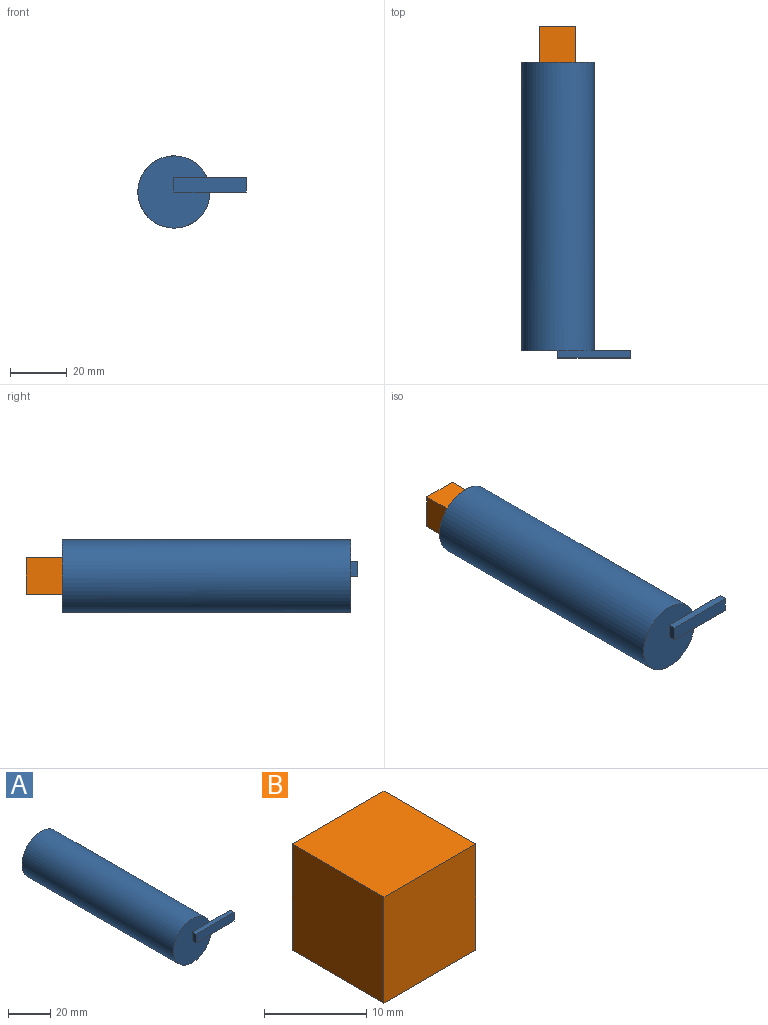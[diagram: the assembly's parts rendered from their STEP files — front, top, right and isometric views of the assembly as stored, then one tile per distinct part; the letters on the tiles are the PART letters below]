
ASSEMBLY  parts=2 mates=1
PART A: 9 faces, bbox 38.1x104.1x25.4 mm
  f0: plane 25.4x25.4mm, normal (0,-1,0), area 444mm2, adj f1,f4,f5,f6
  f1: cylinder r=12.7mm len=101.6mm, axis (0,1,0), area 8107.3mm2, adj f0,f2,f3
  f2: plane 25.4x25.4mm, normal (0,1,0), area 506.7mm2, adj f1
  f3: plane 13.76x5.08mm, normal (0,1,0), area 66.3mm2, adj f1,f4,f6,f7
  f4: plane 25.4x2.54mm, normal (0,0,1), area 64.5mm2, adj f0,f3,f5,f7,f8
  f5: plane 5.08x2.54mm, normal (-1,0,0), area 12.9mm2, adj f0,f4,f6,f8
  f6: plane 25.4x2.54mm, normal (0,0,-1), area 64.5mm2, adj f0,f3,f5,f7,f8
  f7: plane 5.08x2.54mm, normal (1,0,0), area 12.9mm2, adj f3,f4,f6,f8
  f8: plane 25.4x5.08mm, normal (0,-1,0), area 129mm2, adj f4,f5,f6,f7
PART B: 6 faces, bbox 12.7x12.7x12.7 mm
  f0: plane 12.7x12.7mm, normal (0,0,-1), area 161.3mm2, adj f1,f3,f4,f5
  f1: plane 12.7x12.7mm, normal (1,0,0), area 161.3mm2, adj f0,f2,f4,f5
  f2: plane 12.7x12.7mm, normal (0,0,1), area 161.3mm2, adj f1,f3,f4,f5
  f3: plane 12.7x12.7mm, normal (-1,0,0), area 161.3mm2, adj f0,f2,f4,f5
  f4: plane 12.7x12.7mm, normal (0,-1,0), area 161.3mm2, adj f0,f1,f2,f3
  f5: plane 12.7x12.7mm, normal (0,1,0), area 161.3mm2, adj f0,f1,f2,f3
PLACE A t=(-31.2,26.95,-20.34)mm
PLACE B t=(-31.2,39.65,-48.91)mm
MATE slider B.f4 <-> A.f1  axis (0,-1,0) through (-31.2,26.95,-20.34)mm
